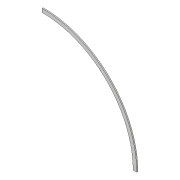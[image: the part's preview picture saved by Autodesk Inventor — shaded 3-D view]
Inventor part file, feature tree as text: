
AUTODESK INVENTOR PART (.ipt)
format: ipt  version: 2018 (Build 220112000, 112)  size: 101,888 bytes
history: native  units: in
note: dims shown in document units (in); Inventor stores cm internally (conversion verified against a paired STEP export)
features: extrude x1, sketch x1
ambient origin geometry x8: Origin, YZ Plane, XZ Plane, XY Plane, X Axis, Y Axis, Z Axis, Center Point
bodies: Solid1 (feature_tree)
feature tree (2):
  extrude  "Extrusion1"  Depth=0.1969in
  sketch  "Sketch1"  dims[d0=31.4961in d1=30.315in d2=0.1969in d3=0.0in]
